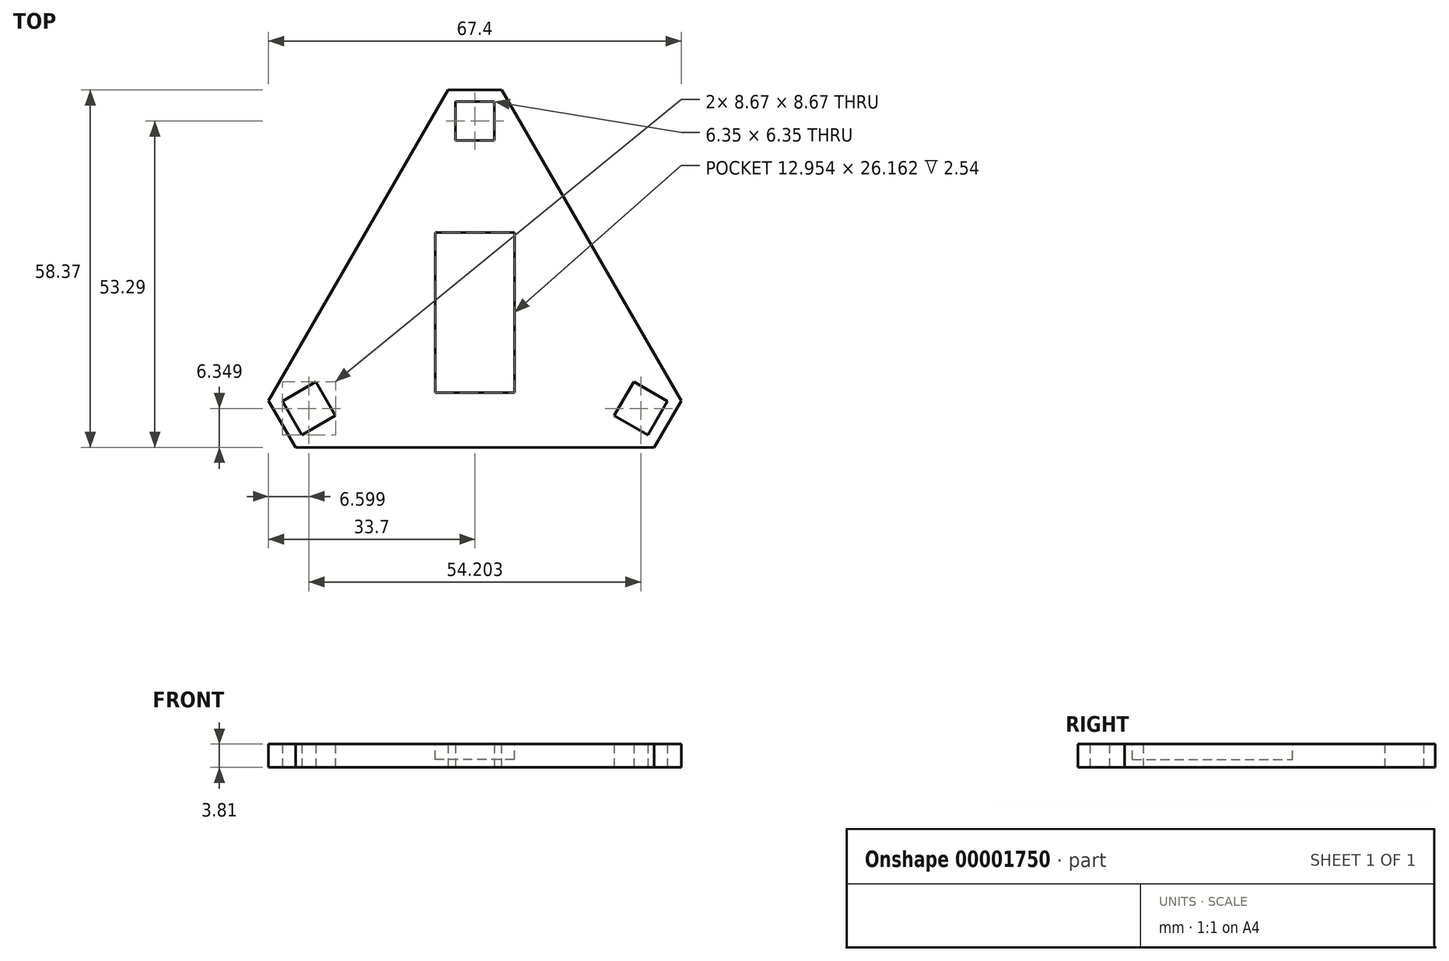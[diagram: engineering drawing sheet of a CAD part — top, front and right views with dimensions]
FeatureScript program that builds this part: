
annotation { "Feature Type Name" : "Feature", "Feature Type Description" : "" }
export const myFeature = defineFeature(function(context is Context, id is Id, definition is map)
    precondition{}
    {
        {
            var Q0;
            Q0=qCreatedBy(makeId("Top.planeOp"),FACE);
            var sketch = newSketch(context, id + "F0", { "sketchPlane" : qUnion([Q0])});
            skLineSegment(sketch, "E0", {"start": v(0, 0) * mm, "end": v(38.1, -66) * mm});
            skLineSegment(sketch, "E1", {"start": v(38.1, -66) * mm, "end": v(-38.1, -66) * mm});
            skLineSegment(sketch, "E2", {"start": v(-38.1, -66) * mm, "end": v(0, 0) * mm});
            skLineSegment(sketch, "E3", {"start": v(0, 0) * mm, "end": v(0, -66) * mm, "construction": true});
            skSolve(sketch);
        }
        {
            var Q0;
            Q0=makeQuery(id+"F0.imprint","IMPRINT",FACE,{"disambiguationData":[TD([[makeQuery(id+"F0.imprint","IMPRINT",EDGE,{"derivedFrom":sQuery(id+"F0.wireOp",EDGE,"E0")}),-1.0]])]});
            extrude(context, id + "F1", {"entities" : qUnion([Q0]), "depth" : 3.8 * mm});
        }
        {
            var Q0;
            Q0=makeQuery(id+"F1.opExtrude","CAP_FACE",FACE,{"disambiguationData":[OSD([sQuery(id+"F0.wireOp",EDGE,"E0"),sQuery(id+"F0.wireOp",EDGE,"E1"),sQuery(id+"F0.wireOp",EDGE,"E2")])],"isStart":false});
            var sketch = newSketch(context, id + "F2", { "sketchPlane" : qUnion([Q0])});
            skLineSegment(sketch, "E4", {"start": v(0, -44) * mm, "end": v(0, -66) * mm, "construction": true});
            skLineSegment(sketch, "E5.rect.bottom", {"start": v(6.48, -57.08) * mm, "end": v(-6.48, -57.08) * mm});
            skLineSegment(sketch, "E5.rect.top", {"start": v(6.48, -30.91) * mm, "end": v(-6.48, -30.91) * mm});
            skLineSegment(sketch, "E5.rect.left", {"start": v(6.48, -57.08) * mm, "end": v(6.48, -30.91) * mm});
            skLineSegment(sketch, "E5.rect.right", {"start": v(-6.48, -57.08) * mm, "end": v(-6.48, -30.91) * mm});
            skPoint(sketch, "E5.rect.middle", {"position": v(0, -44) * mm});
            skLineSegment(sketch, "E6", {"start": v(38.1, -66) * mm, "end": v(0, -44) * mm, "construction": true});
            skLineSegment(sketch, "E7", {"start": v(0, -44) * mm, "end": v(19.05, -33) * mm, "construction": true});
            skPoint(sketch, "E8.orphan", {"position": v(-19.05, -33) * mm});
            skPoint(sketch, "E9.orphan", {"position": v(0, 0) * mm});
            skSolve(sketch);
        }
        {
            var Q0;
            Q0 = qSketchRegion(id + "F2", true);
            extrude(context, id + "F3", {"entities" : qUnion([Q0]), "operationType" : NewBodyOperationType.REMOVE, "oppositeDirection" : true, "depth" : 2.54 * mm});
        }
        {
            var Q0;
            Q0=qCreatedBy(makeId("Top.planeOp"),FACE);
            var sketch = newSketch(context, id + "F4", { "sketchPlane" : qUnion([Q0])});
            skLineSegment(sketch, "E10", {"start": v(0, 0) * mm, "end": v(0, -12.7) * mm, "construction": true});
            skLineSegment(sketch, "E11.1.0", {"start": v(-38.1, -66) * mm, "end": v(-27.1, -59.64) * mm, "construction": true});
            skLineSegment(sketch, "E11.2.0", {"start": v(38.1, -66) * mm, "end": v(27.1, -59.64) * mm, "construction": true});
            skPoint(sketch, "E11.center", {"position": v(0, -44) * mm});
            skLineSegment(sketch, "E12.rect.bottom", {"start": v(3.18, -15.88) * mm, "end": v(-3.18, -15.88) * mm});
            skLineSegment(sketch, "E12.rect.top", {"start": v(3.18, -9.53) * mm, "end": v(-3.17, -9.53) * mm});
            skLineSegment(sketch, "E12.rect.left", {"start": v(3.18, -15.88) * mm, "end": v(3.18, -9.53) * mm});
            skLineSegment(sketch, "E12.rect.right", {"start": v(-3.18, -15.88) * mm, "end": v(-3.17, -9.53) * mm});
            skPoint(sketch, "E12.rect.middle", {"position": v(0, -12.7) * mm});
            skLineSegment(sketch, "E13.1.0", {"start": v(-31.44, -58.48) * mm, "end": v(-28.26, -63.98) * mm});
            skLineSegment(sketch, "E13.1.1", {"start": v(-25.94, -55.3) * mm, "end": v(-31.44, -58.48) * mm});
            skLineSegment(sketch, "E13.1.2", {"start": v(-25.94, -55.3) * mm, "end": v(-22.76, -60.8) * mm});
            skLineSegment(sketch, "E13.1.3", {"start": v(-22.76, -60.8) * mm, "end": v(-28.26, -63.98) * mm});
            skLineSegment(sketch, "E13.2.0", {"start": v(28.26, -63.98) * mm, "end": v(31.44, -58.48) * mm});
            skLineSegment(sketch, "E13.2.1", {"start": v(22.76, -60.8) * mm, "end": v(28.26, -63.98) * mm});
            skLineSegment(sketch, "E13.2.2", {"start": v(22.76, -60.8) * mm, "end": v(25.94, -55.3) * mm});
            skLineSegment(sketch, "E13.2.3", {"start": v(25.94, -55.3) * mm, "end": v(31.44, -58.48) * mm});
            skSolve(sketch);
        }
        {
            var Q0;
            Q0 = qSketchRegion(id + "F4", true);
            extrude(context, id + "F5", {"entities" : qUnion([Q0]), "operationType" : NewBodyOperationType.REMOVE, "depth" : 3.8 * mm});
        }
        {
            var Q0;
            Q0=makeQuery(id+"F1.opExtrude","SWEPT_EDGE",EDGE,{"disambiguationData":[OSD([sQuery(id+"F0.wireOp",EDGE,"E1"),sQuery(id+"F0.wireOp",EDGE,"E2")])]});
            var Q1;
            Q1=makeQuery(id+"F1.opExtrude","SWEPT_EDGE",EDGE,{"disambiguationData":[OSD([sQuery(id+"F0.wireOp",EDGE,"E0"),sQuery(id+"F0.wireOp",EDGE,"E2")])]});
            var Q2;
            Q2=makeQuery(id+"F1.opExtrude","SWEPT_EDGE",EDGE,{"disambiguationData":[OSD([sQuery(id+"F0.wireOp",EDGE,"E0"),sQuery(id+"F0.wireOp",EDGE,"E1")])]});
            chamfer(context, id + "F6", {"entities" : qUnion([Q0, Q1, Q2]), "width" : 5.08 * mm, "tangentPropagation" : true});
        }
    });
